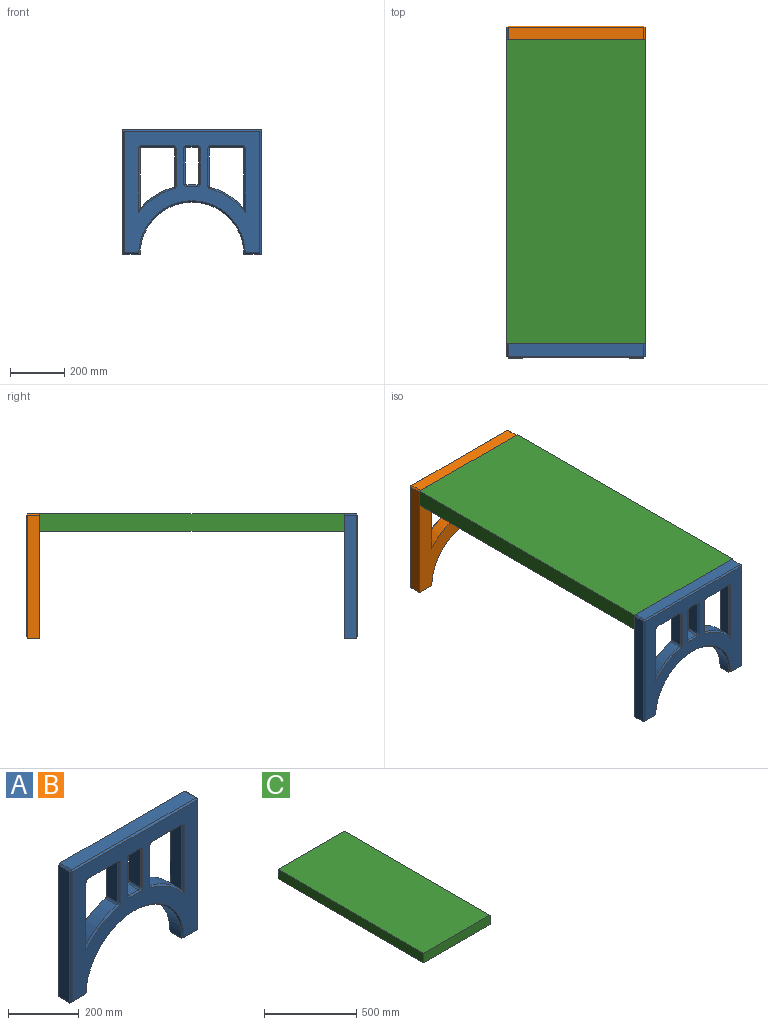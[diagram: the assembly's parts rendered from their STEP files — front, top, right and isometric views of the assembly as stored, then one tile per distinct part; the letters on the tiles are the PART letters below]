
ASSEMBLY  parts=3 mates=4
PART A: 62 faces, bbox 508x50.8x457.2 mm
  f0: cylinder r=6.35mm len=45.72mm, axis (0,1,0), area 377.2mm2, adj f1,f27,f29,f40
  f1: plane 135.75x45.72mm, normal (1,0,0), area 6206.3mm2, adj f0,f2,f29,f41
  f2: cylinder r=6.35mm len=45.72mm, axis (0,1,0), area 456mm2, adj f1,f3,f29,f43
  f3: plane 114.3x45.72mm, normal (0,0,-1), area 5225.8mm2, adj f2,f4,f29,f45
  f4: cylinder r=6.35mm len=45.72mm, axis (0,1,0), area 456mm2, adj f3,f5,f29,f46
  f5: plane 218.54x45.72mm, normal (-1,0,0), area 9991.9mm2, adj f4,f27,f29,f44
  f6: cylinder r=6.35mm len=45.72mm, axis (0,1,0), area 477.3mm2, adj f7,f24,f29,f54
  f7: cylinder r=253.73mm len=45.72mm, axis (0,1,0), area 1700.9mm2, adj f6,f8,f29,f56
  f8: cylinder r=6.35mm len=45.72mm, axis (0,1,0), area 477.3mm2, adj f7,f9,f29,f58
  f9: plane 126.76x45.72mm, normal (1,0,0), area 5795.6mm2, adj f8,f10,f29,f60
  f10: cylinder r=6.35mm len=45.72mm, axis (0,1,0), area 456mm2, adj f9,f11,f29,f61
  f11: plane 45.72x38.1mm, normal (0,0,-1), area 1741.9mm2, adj f10,f12,f29,f59
  f12: cylinder r=6.35mm len=45.72mm, axis (0,1,0), area 456mm2, adj f11,f24,f29,f57
  f13: plane 63.5x45.72mm, normal (0,0,-1), area 2903.2mm2, adj f14,f25,f29,f30
  f14: cylinder r=190.5mm len=381mm, axis (0,1,0), area 27435.4mm2, adj f13,f15,f29,f31
  f15: plane 63.5x45.72mm, normal (0,0,-1), area 2903.2mm2, adj f14,f16,f29,f34
  f16: plane 452.12x45.72mm, normal (1,0,0), area 20670.9mm2, adj f15,f29,f36,f39
  f17: plane 497.84x45.72mm, normal (0,0,1), area 22761.2mm2, adj f29,f33,f37,f39
  f18: cylinder r=6.35mm len=45.72mm, axis (0,1,0), area 377.2mm2, adj f19,f26,f29,f48
  f19: cylinder r=254mm len=122.35mm, axis (0,1,0), area 6694.1mm2, adj f18,f20,f29,f50
  f20: plane 218.54x45.72mm, normal (1,0,0), area 9991.9mm2, adj f19,f21,f29,f52
  f21: cylinder r=6.35mm len=45.72mm, axis (0,1,0), area 456mm2, adj f20,f22,f29,f53
  f22: plane 114.3x45.72mm, normal (0,0,-1), area 5225.8mm2, adj f21,f23,f29,f51
  f23: cylinder r=6.35mm len=45.72mm, axis (0,1,0), area 456mm2, adj f22,f26,f29,f49
  f24: plane 126.76x45.72mm, normal (-1,0,0), area 5795.6mm2, adj f6,f12,f29,f55
  f25: plane 452.12x45.72mm, normal (-1,0,0), area 20670.9mm2, adj f13,f29,f32,f33
  f26: plane 135.75x45.72mm, normal (-1,0,0), area 6206.3mm2, adj f18,f23,f29,f47
  f27: cylinder r=254mm len=122.35mm, axis (0,1,0), area 6694.1mm2, adj f0,f5,f29,f42
  f28: plane 497.84x447.04mm, normal (0,-1,0), area 103423.6mm2, adj f30,f31,f32,f34,f36,f37,f40,f41
  f29: plane 508x457.2mm, normal (0,1,0), area 122936.5mm2, adj f0,f1,f2,f3,f4,f5,f6,f7
  f30: plane 63.5x5.08mm, normal (0,-0.71,-0.71), area 419.8mm2, adj f13,f28,f31,f32
  f31: cone r=190.5mm half-angle=45deg, axis (0,-1,0), area 4331.9mm2, adj f14,f28,f30,f34
  f32: plane 452.12x5.08mm, normal (-0.71,-0.71,0), area 3229.9mm2, adj f25,f28,f30,f35
  f33: plane 45.72x5.08mm, normal (-0.71,0,0.71), area 328.5mm2, adj f17,f25,f29,f35
  f34: plane 63.5x5.08mm, normal (0,-0.71,-0.71), area 419.8mm2, adj f15,f28,f31,f36
  f35: plane 5.08x5.08mm, normal (-0.58,-0.58,0.58), area 22.3mm2, adj f32,f33,f37
  f36: plane 452.12x5.08mm, normal (0.71,-0.71,0), area 3229.9mm2, adj f16,f28,f34,f38
  f37: plane 497.84x5.08mm, normal (0,-0.71,0.71), area 3576.6mm2, adj f17,f28,f35,f38
  f38: plane 5.08x5.08mm, normal (0.58,-0.58,0.58), area 22.3mm2, adj f36,f37,f39
  f39: plane 45.72x5.08mm, normal (0.71,0,0.71), area 328.5mm2, adj f16,f17,f29,f38
  f40: cone r=6.35mm half-angle=45deg, axis (0,-1,0), area 83mm2, adj f0,f28,f41,f42
  f41: plane 135.75x5.08mm, normal (0.71,-0.71,0), area 975.2mm2, adj f1,f28,f40,f43
  f42: cone r=254mm half-angle=45deg, axis (0,1,0), area 1090.7mm2, adj f27,f28,f40,f44
  f43: cone r=6.35mm half-angle=45deg, axis (0,-1,0), area 100.3mm2, adj f2,f28,f41,f45
  f44: plane 232.57x5.08mm, normal (-0.71,-0.71,0), area 1619.7mm2, adj f5,f28,f42,f46
  f45: plane 114.3x5.08mm, normal (0,-0.71,-0.71), area 821.2mm2, adj f3,f28,f43,f46
  f46: cone r=6.35mm half-angle=45deg, axis (0,-1,0), area 100.3mm2, adj f4,f28,f44,f45
  f47: plane 135.75x5.08mm, normal (-0.71,-0.71,0), area 975.2mm2, adj f26,f28,f48,f49
  f48: cone r=6.35mm half-angle=45deg, axis (0,-1,0), area 83mm2, adj f18,f28,f47,f50
  f49: cone r=6.35mm half-angle=45deg, axis (0,-1,0), area 100.3mm2, adj f23,f28,f47,f51
  f50: cone r=248.92mm half-angle=45deg, axis (0,1,0), area 1090.7mm2, adj f19,f28,f48,f52
  f51: plane 114.3x5.08mm, normal (0,-0.71,-0.71), area 821.2mm2, adj f22,f28,f49,f53
  f52: plane 232.57x5.08mm, normal (0.71,-0.71,0), area 1619.7mm2, adj f20,f28,f50,f53
  f53: cone r=6.35mm half-angle=45deg, axis (0,-1,0), area 100.3mm2, adj f21,f28,f51,f52
  f54: cone r=6.35mm half-angle=45deg, axis (0,-1,0), area 105mm2, adj f6,f28,f55,f56
  f55: plane 126.76x5.08mm, normal (-0.71,-0.71,0), area 910.7mm2, adj f24,f28,f54,f57
  f56: cone r=248.65mm half-angle=45deg, axis (0,1,0), area 264.6mm2, adj f7,f28,f54,f58
  f57: cone r=6.35mm half-angle=45deg, axis (0,-1,0), area 100.3mm2, adj f12,f28,f55,f59
  f58: cone r=6.35mm half-angle=45deg, axis (0,-1,0), area 105mm2, adj f8,f28,f56,f60
  f59: plane 38.1x5.08mm, normal (0,-0.71,-0.71), area 273.7mm2, adj f11,f28,f57,f61
  f60: plane 126.76x5.08mm, normal (0.71,-0.71,0), area 910.7mm2, adj f9,f28,f58,f61
  f61: cone r=6.35mm half-angle=45deg, axis (0,-1,0), area 100.3mm2, adj f10,f28,f59,f60
PART B: same geometry as A
PART C: 6 faces, bbox 508x1117.6x63.5 mm
  f0: plane 508x63.5mm, normal (0,-1,0), area 32258mm2, adj f1,f3,f4,f5
  f1: plane 1117.6x63.5mm, normal (1,0,0), area 70967.6mm2, adj f0,f2,f4,f5
  f2: plane 508x63.5mm, normal (0,1,0), area 32258mm2, adj f1,f3,f4,f5
  f3: plane 1117.6x63.5mm, normal (-1,0,0), area 70967.6mm2, adj f0,f2,f4,f5
  f4: plane 1117.6x508mm, normal (0,0,1), area 567740.8mm2, adj f0,f1,f2,f3
  f5: plane 1117.6x508mm, normal (0,0,-1), area 567740.8mm2, adj f0,f1,f2,f3
PLACE A t=(-198.12,-287.77,34.27)mm
PLACE B rot(axis=(0,0,1),180deg) t=(-198.12,829.83,34.27)mm
PLACE C t=(-198.12,271.03,199.37)mm
MATE parallel A.f29 <-> C.f0  axis (0,1,0) through (-198.12,-287.77,262.87)mm
MATE parallel B.f17 <-> C.f5  axis (0,0,1) through (50.8,875.55,262.87)mm
MATE parallel A.f17 <-> C.f5  axis (0,0,1) through (50.8,-333.49,262.87)mm
MATE parallel B.f29 <-> C.f2  axis (0,-1,0) through (-198.12,829.83,262.87)mm
